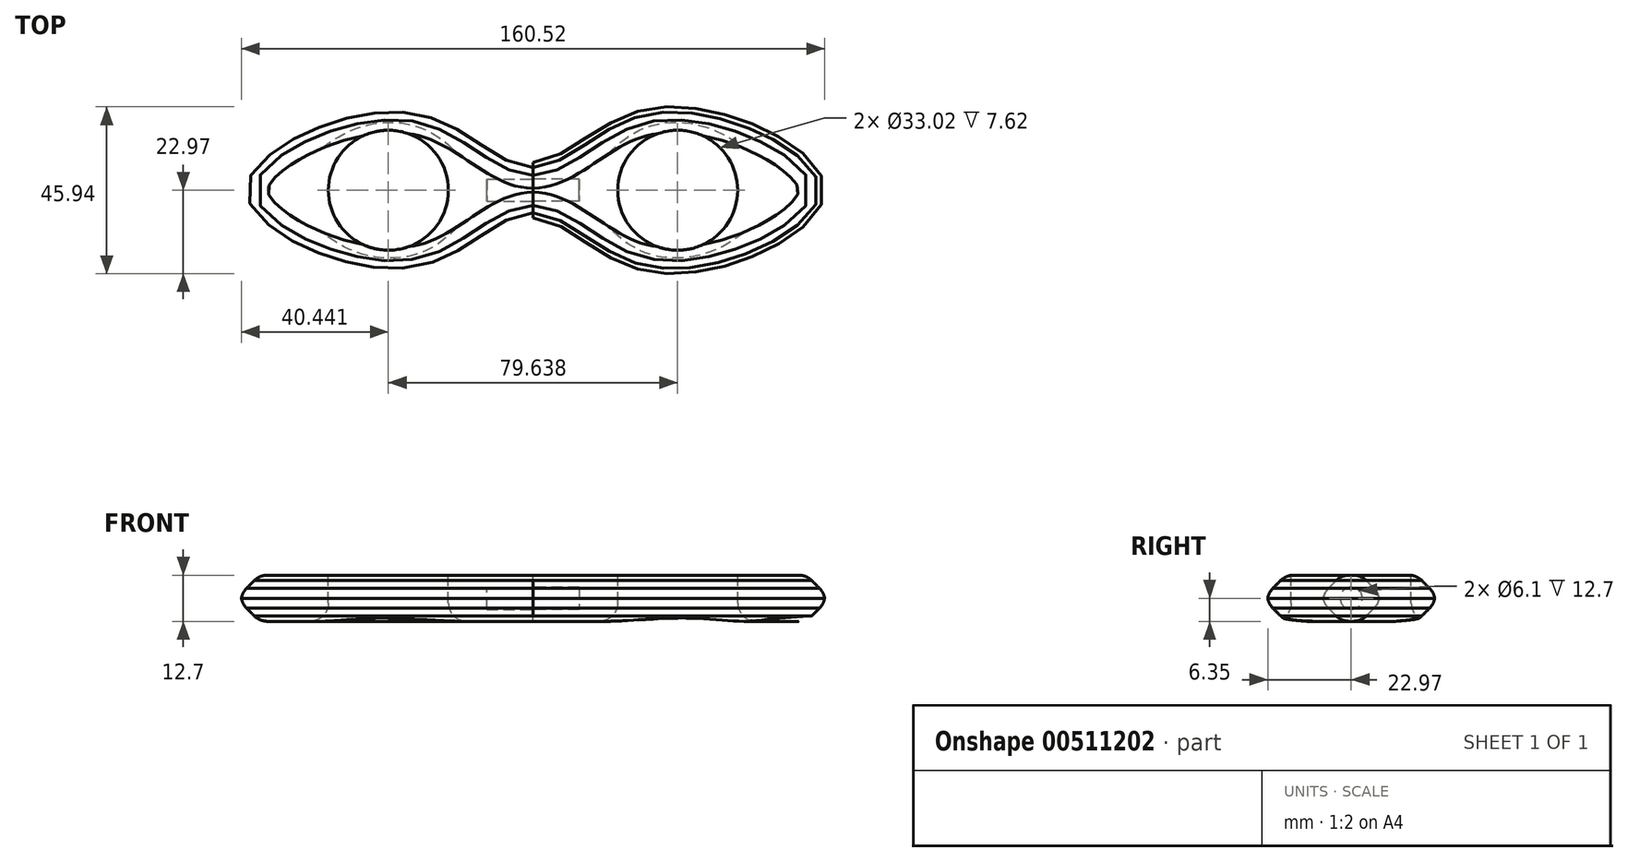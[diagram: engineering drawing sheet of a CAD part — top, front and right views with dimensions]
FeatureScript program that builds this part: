
annotation { "Feature Type Name" : "Feature", "Feature Type Description" : "" }
export const myFeature = defineFeature(function(context is Context, id is Id, definition is map)
    precondition{}
    {
        {
            var Q0;
            Q0=qCreatedBy(makeId("Top.planeOp"),FACE);
            var sketch = newSketch(context, id + "F0", { "sketchPlane" : qUnion([Q0])});
            skLineSegment(sketch, "E0.bottom", {"start": v(-76.92, 22.27) * mm, "end": v(76.92, 22.27) * mm, "construction": true});
            skLineSegment(sketch, "E0.top", {"start": v(-76.92, -22.27) * mm, "end": v(76.92, -22.27) * mm, "construction": true});
            skLineSegment(sketch, "E0.left", {"start": v(-76.92, 22.27) * mm, "end": v(-76.92, -22.27) * mm, "construction": true});
            skLineSegment(sketch, "E0.right", {"start": v(76.92, 22.27) * mm, "end": v(76.92, -22.27) * mm, "construction": true});
            skPoint(sketch, "E0.middle", {"position": v(0, 0) * mm});
            skLineSegment(sketch, "E1.bottom", {"start": v(-76.92, 7.72) * mm, "end": v(76.92, 7.72) * mm, "construction": true});
            skLineSegment(sketch, "E1.top", {"start": v(-76.92, -7.72) * mm, "end": v(76.92, -7.72) * mm, "construction": true});
            skLineSegment(sketch, "E1.left", {"start": v(-76.92, 7.72) * mm, "end": v(-76.92, -7.72) * mm, "construction": true});
            skLineSegment(sketch, "E1.right", {"start": v(76.92, 7.72) * mm, "end": v(76.92, -7.72) * mm, "construction": true});
            skLineSegment(sketch, "E2.bottom", {"start": v(30.74, 22.27) * mm, "end": v(-30.74, 22.27) * mm, "construction": true});
            skLineSegment(sketch, "E2.top", {"start": v(30.74, -22.27) * mm, "end": v(-30.74, -22.27) * mm, "construction": true});
            skLineSegment(sketch, "E2.left", {"start": v(30.74, 22.27) * mm, "end": v(30.74, -22.27) * mm, "construction": true});
            skLineSegment(sketch, "E2.right", {"start": v(-30.74, 22.27) * mm, "end": v(-30.74, -22.27) * mm, "construction": true});
            skFitSpline(sketch, "E3", {"points": [v(-76.92, 7.72) * mm, v(-30.74, 22.27) * mm, v(0, 7.72) * mm, v(30.74, 22.27) * mm, v(76.92, 7.72) * mm, v(76.92, -7.72) * mm, v(30.74, -22.27) * mm, v(0, -7.72) * mm, v(-30.74, -22.27) * mm, v(-76.92, -7.72) * mm, v(-76.92, 7.72) * mm]});
            skLineSegment(sketch, "E4", {"start": v(0, 7.72) * mm, "end": v(0, -7.72) * mm});
            skSolve(sketch);
        }
        {
            var Q0;
            {var subQ0=sQuery(id+"F0.wireOp",EDGE,"E4");Q0=makeQuery(id+"F0.imprint","IMPRINT",FACE,{"disambiguationData":[TD([[makeQuery(id+"F0.imprint","IMPRINT",EDGE,{"derivedFrom":subQ0}),-1.0]])]});}
            extrude(context, id + "F1", {"entities" : qUnion([Q0]), "depth" : 12.7 * mm});
        }
        {
            var Q0;
            {var subQ0=sQuery(id+"F0.wireOp",EDGE,"E4");Q0=makeQuery(id+"F0.imprint","IMPRINT",FACE,{"disambiguationData":[TD([[makeQuery(id+"F0.imprint","IMPRINT",EDGE,{"derivedFrom":subQ0}),1.0]])]});}
            extrude(context, id + "F2", {"entities" : qUnion([Q0]), "depth" : 12.7 * mm});
        }
        {
            var Q0;
            Q0=makeQuery(id+"F1.opExtrude","CAP_FACE",FACE,{"disambiguationData":[OSD([sQuery(id+"F0.wireOp",EDGE,"E3"),sQuery(id+"F0.wireOp",EDGE,"E4")])],"isStart":false});
            var sketch = newSketch(context, id + "F3", { "sketchPlane" : qUnion([Q0])});
            skLineSegment(sketch, "E5", {"start": v(0, 50.05) * mm, "end": v(0, -54.86) * mm, "construction": true});
            skCircle(sketch, "E6", {"center": v(-39.82, 0) * mm, "radius": 16.51 * mm});
            skCircle(sketch, "E7.MirrorC", {"center": v(39.82, 0) * mm, "radius": 16.51 * mm});
            skSolve(sketch);
        }
        {
            var Q0;
            Q0=qSketchRegion(id+"F3",true);
            extrude(context, id + "F4", {"entities" : qUnion([Q0]), "operationType" : NewBodyOperationType.REMOVE, "endBound" : BoundingType.THROUGH_ALL, "oppositeDirection" : true, "depth" : 25.4 * mm});
        }
        {
            var Q0;
            Q0=makeQuery(id+"F1.opExtrude","CAP_EDGE",EDGE,{"disambiguationData":[OSD([sQuery(id+"F0.wireOp",EDGE,"E3")])],"isStart":false});
            chamfer(context, id + "F5", {"entities" : qUnion([Q0]), "width" : 5.08 * mm, "tangentPropagation" : true});
        }
        {
            var Q0;
            {var subQ0=sQuery(id+"F0.wireOp",EDGE,"E3");Q0=makeQuery(id+"F5.opChamfer","BLEND_EDGE",EDGE,{"blendedFrom":[makeQuery(id+"F1.opExtrude","CAP_EDGE",EDGE,{"disambiguationData":[OSD([subQ0])],"isStart":false}),makeQuery(id+"F1.opExtrude","SWEPT_FACE",FACE,{"disambiguationData":[OSD([subQ0])]})],"blendedInto":[makeQuery(id+"F1.opExtrude","SWEPT_FACE",FACE,{"disambiguationData":[OSD([subQ0])]})]});}
            var Q1;
            {var subQ0=sQuery(id+"F0.wireOp",EDGE,"E3");Q1=makeQuery(id+"F5.opChamfer","BLEND_EDGE",EDGE,{"blendedFrom":[makeQuery(id+"F1.opExtrude","CAP_EDGE",EDGE,{"disambiguationData":[OSD([subQ0])],"isStart":false}),makeQuery(id+"F1.opExtrude","CAP_FACE",FACE,{"disambiguationData":[OSD([subQ0,sQuery(id+"F0.wireOp",EDGE,"E4")])],"isStart":false})],"blendedInto":[makeQuery(id+"F1.opExtrude","CAP_FACE",FACE,{"disambiguationData":[OSD([subQ0,sQuery(id+"F0.wireOp",EDGE,"E4")])],"isStart":false})]});}
            var Q2;
            Q2=makeQuery(id+"F4.boolean.opBoolean","COPY",EDGE,{"derivedFrom":makeQuery(id+"F4.opExtrude","CAP_EDGE",EDGE,{"disambiguationData":[OSD([sQuery(id+"F3.wireOp",EDGE,"E6")])],"isStart":true})});
            fillet(context, id + "F6", {"entities" : qUnion([Q0, Q1, Q2]), "radius" : 5.08 * mm, "tangentPropagation" : true, "allowEdgeOverflow" : false});
        }
        {
            var Q0;
            Q0=makeQuery(id+"F2.opExtrude","CAP_EDGE",EDGE,{"disambiguationData":[OSD([sQuery(id+"F0.wireOp",EDGE,"E3")])],"isStart":false});
            chamfer(context, id + "F7", {"entities" : qUnion([Q0]), "width" : 5.08 * mm, "tangentPropagation" : true});
        }
        {
            var Q0;
            {var subQ0=sQuery(id+"F0.wireOp",EDGE,"E3");Q0=makeQuery(id+"F7.opChamfer","BLEND_EDGE",EDGE,{"blendedFrom":[makeQuery(id+"F2.opExtrude","CAP_EDGE",EDGE,{"disambiguationData":[OSD([subQ0])],"isStart":false}),makeQuery(id+"F2.opExtrude","SWEPT_FACE",FACE,{"disambiguationData":[OSD([subQ0])]})],"blendedInto":[makeQuery(id+"F2.opExtrude","SWEPT_FACE",FACE,{"disambiguationData":[OSD([subQ0])]})]});}
            var Q1;
            Q1=makeQuery(id+"F4.boolean.opBoolean","COPY",EDGE,{"derivedFrom":makeQuery(id+"F4.opExtrude","CAP_EDGE",EDGE,{"disambiguationData":[OSD([sQuery(id+"F3.wireOp",EDGE,"E7.MirrorC")])],"isStart":true})});
            var Q2;
            {var subQ0=sQuery(id+"F0.wireOp",EDGE,"E3");Q2=makeQuery(id+"F7.opChamfer","BLEND_EDGE",EDGE,{"blendedFrom":[makeQuery(id+"F2.opExtrude","CAP_EDGE",EDGE,{"disambiguationData":[OSD([subQ0])],"isStart":false}),makeQuery(id+"F2.opExtrude","CAP_FACE",FACE,{"disambiguationData":[OSD([subQ0,sQuery(id+"F0.wireOp",EDGE,"E4")])],"isStart":false})],"blendedInto":[makeQuery(id+"F2.opExtrude","CAP_FACE",FACE,{"disambiguationData":[OSD([subQ0,sQuery(id+"F0.wireOp",EDGE,"E4")])],"isStart":false})]});}
            fillet(context, id + "F8", {"entities" : qUnion([Q0, Q1, Q2]), "radius" : 5.08 * mm, "tangentPropagation" : true, "allowEdgeOverflow" : false});
        }
        {
            var Q0;
            Q0=makeQuery(id+"F1.opExtrude","CAP_EDGE",EDGE,{"disambiguationData":[OSD([sQuery(id+"F0.wireOp",EDGE,"E3")])],"isStart":true});
            var Q1;
            Q1=makeQuery(id+"F2.opExtrude","CAP_EDGE",EDGE,{"disambiguationData":[OSD([sQuery(id+"F0.wireOp",EDGE,"E3")])],"isStart":true});
            chamfer(context, id + "F9", {"entities" : qUnion([Q0, Q1]), "width" : 5.08 * mm, "tangentPropagation" : true});
        }
        {
            var Q0;
            {var subQ0=sQuery(id+"F0.wireOp",EDGE,"E3");Q0=makeQuery(id+"F9.opChamfer","BLEND_EDGE",EDGE,{"blendedFrom":[makeQuery(id+"F1.opExtrude","CAP_EDGE",EDGE,{"disambiguationData":[OSD([subQ0])],"isStart":true}),makeQuery(id+"F1.opExtrude","SWEPT_FACE",FACE,{"disambiguationData":[OSD([subQ0])]})],"blendedInto":[makeQuery(id+"F1.opExtrude","SWEPT_FACE",FACE,{"disambiguationData":[OSD([subQ0])]})]});}
            var Q1;
            {var subQ0=sQuery(id+"F0.wireOp",EDGE,"E3");Q1=makeQuery(id+"F9.opChamfer","BLEND_EDGE",EDGE,{"blendedFrom":[makeQuery(id+"F2.opExtrude","CAP_EDGE",EDGE,{"disambiguationData":[OSD([subQ0])],"isStart":true}),makeQuery(id+"F2.opExtrude","SWEPT_FACE",FACE,{"disambiguationData":[OSD([subQ0])]})],"blendedInto":[makeQuery(id+"F2.opExtrude","SWEPT_FACE",FACE,{"disambiguationData":[OSD([subQ0])]})]});}
            var Q2;
            {var subQ0=sQuery(id+"F0.wireOp",EDGE,"E3");Q2=makeQuery(id+"F9.opChamfer","BLEND_EDGE",EDGE,{"blendedFrom":[makeQuery(id+"F1.opExtrude","CAP_EDGE",EDGE,{"disambiguationData":[OSD([subQ0])],"isStart":true}),makeQuery(id+"F1.opExtrude","CAP_FACE",FACE,{"disambiguationData":[OSD([subQ0,sQuery(id+"F0.wireOp",EDGE,"E4")])],"isStart":true})],"blendedInto":[makeQuery(id+"F1.opExtrude","CAP_FACE",FACE,{"disambiguationData":[OSD([subQ0,sQuery(id+"F0.wireOp",EDGE,"E4")])],"isStart":true})]});}
            var Q3;
            {var subQ0=sQuery(id+"F0.wireOp",EDGE,"E3");Q3=makeQuery(id+"F9.opChamfer","BLEND_EDGE",EDGE,{"blendedFrom":[makeQuery(id+"F2.opExtrude","CAP_EDGE",EDGE,{"disambiguationData":[OSD([subQ0])],"isStart":true}),makeQuery(id+"F2.opExtrude","CAP_FACE",FACE,{"disambiguationData":[OSD([subQ0,sQuery(id+"F0.wireOp",EDGE,"E4")])],"isStart":true})],"blendedInto":[makeQuery(id+"F2.opExtrude","CAP_FACE",FACE,{"disambiguationData":[OSD([subQ0,sQuery(id+"F0.wireOp",EDGE,"E4")])],"isStart":true})]});}
            var Q4;
            Q4=makeQuery(id+"F4.boolean.opBoolean","INTERSECT",EDGE,{"derivedFrom":[makeQuery(id+"F2.opExtrude","CAP_FACE",FACE,{"disambiguationData":[OSD([sQuery(id+"F0.wireOp",EDGE,"E3"),sQuery(id+"F0.wireOp",EDGE,"E4")])],"isStart":true}),makeQuery(id+"F4.opExtrude","SWEPT_FACE",FACE,{"disambiguationData":[OSD([sQuery(id+"F3.wireOp",EDGE,"E7.MirrorC")])]})]});
            var Q5;
            Q5=makeQuery(id+"F4.boolean.opBoolean","INTERSECT",EDGE,{"derivedFrom":[makeQuery(id+"F1.opExtrude","CAP_FACE",FACE,{"disambiguationData":[OSD([sQuery(id+"F0.wireOp",EDGE,"E3"),sQuery(id+"F0.wireOp",EDGE,"E4")])],"isStart":true}),makeQuery(id+"F4.opExtrude","SWEPT_FACE",FACE,{"disambiguationData":[OSD([sQuery(id+"F3.wireOp",EDGE,"E6")])]})]});
            fillet(context, id + "F10", {"entities" : qUnion([Q0, Q1, Q2, Q3, Q4, Q5]), "radius" : 5.08 * mm, "tangentPropagation" : true, "allowEdgeOverflow" : false});
        }
        {
            var Q0;
            Q0=makeQuery(id+"F1.opExtrude","SWEPT_FACE",FACE,{"disambiguationData":[OSD([sQuery(id+"F0.wireOp",EDGE,"E4")])]});
            var sketch = newSketch(context, id + "F11", { "sketchPlane" : qUnion([Q0])});
            skCircle(sketch, "E8", {"center": v(0, 6.35) * mm, "radius": 3.05 * mm});
            skSolve(sketch);
        }
        {
            var Q0;
            Q0=qSketchRegion(id+"F11",true);
            extrude(context, id + "F12", {"entities" : qUnion([Q0]), "operationType" : NewBodyOperationType.REMOVE, "oppositeDirection" : true, "depth" : 12.7 * mm});
        }
        {
            var Q0;
            Q0=makeQuery(id+"F2.opExtrude","SWEPT_FACE",FACE,{"disambiguationData":[OSD([sQuery(id+"F0.wireOp",EDGE,"E4")])]});
            var sketch = newSketch(context, id + "F13", { "sketchPlane" : qUnion([Q0])});
            skCircle(sketch, "E9", {"center": v(0, 6.35) * mm, "radius": 3.05 * mm});
            skSolve(sketch);
        }
        {
            var Q0;
            Q0=qSketchRegion(id+"F13",true);
            extrude(context, id + "F14", {"entities" : qUnion([Q0]), "operationType" : NewBodyOperationType.REMOVE, "oppositeDirection" : true, "depth" : 12.7 * mm});
        }
    });
